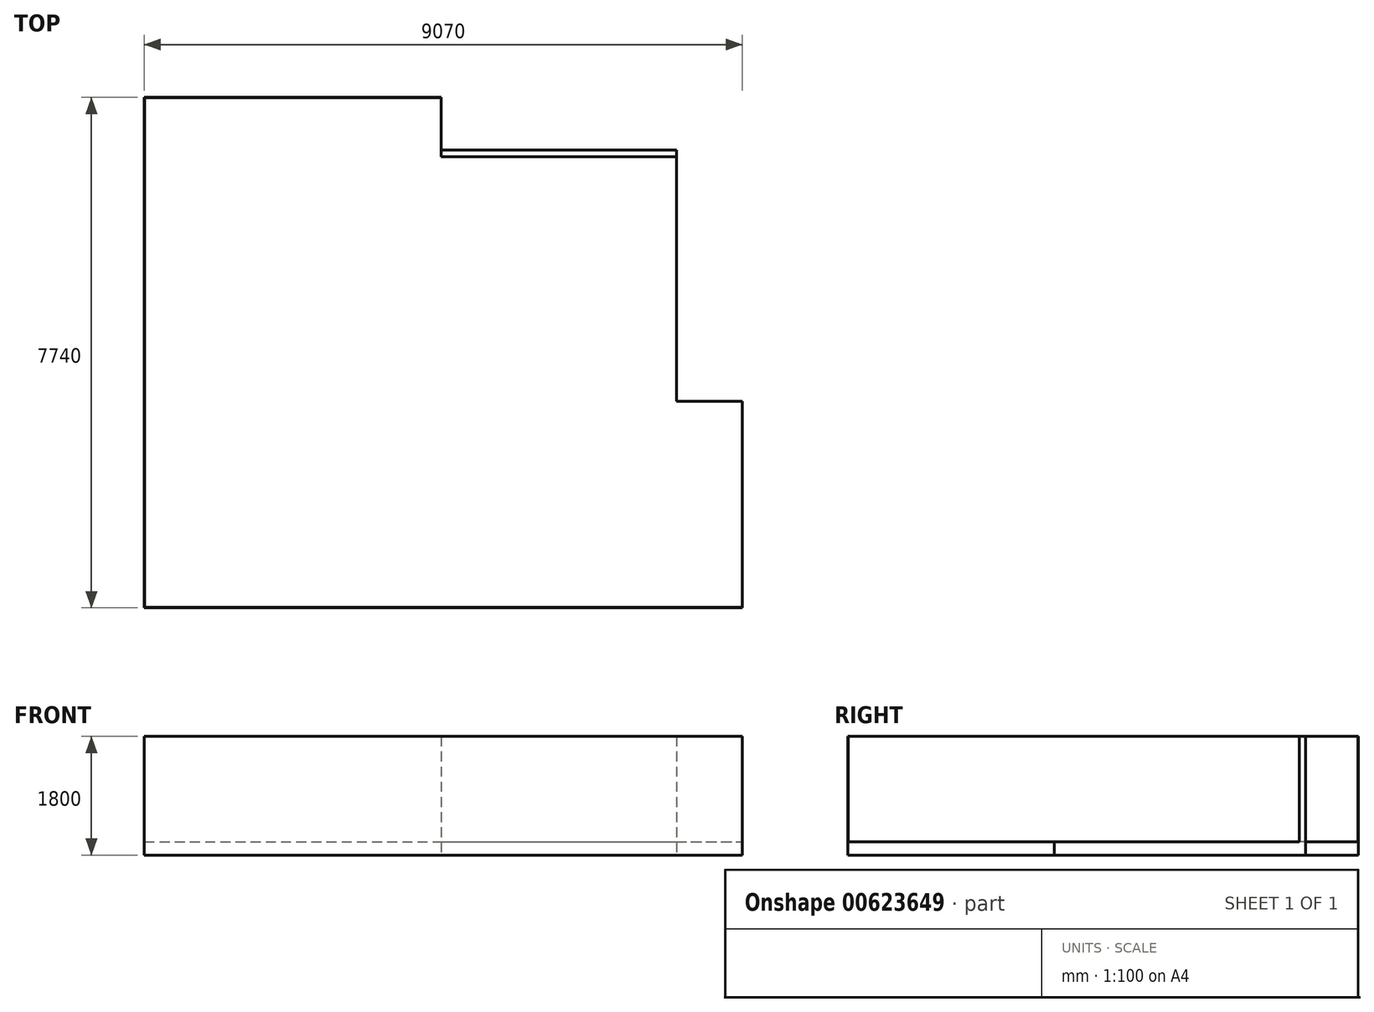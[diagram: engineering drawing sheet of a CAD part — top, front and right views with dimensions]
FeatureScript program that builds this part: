
annotation { "Feature Type Name" : "Feature", "Feature Type Description" : "" }
export const myFeature = defineFeature(function(context is Context, id is Id, definition is map)
    precondition{}
    {
        {
            var Q0;
            Q0=qCreatedBy(makeId("Top.planeOp"),FACE);
            var sketch = newSketch(context, id + "F0", { "sketchPlane" : qUnion([Q0])});
            skLineSegment(sketch, "E0", {"start": v(-109.76, -3110.31) * mm, "end": v(-109.76, 4629.69) * mm});
            skLineSegment(sketch, "E1", {"start": v(-109.76, -3110.31) * mm, "end": v(8960.24, -3110.31) * mm});
            skLineSegment(sketch, "E2", {"start": v(-109.76, 4629.69) * mm, "end": v(4390.24, 4629.69) * mm});
            skLineSegment(sketch, "E3", {"start": v(4390.24, 4629.69) * mm, "end": v(4390.24, 3729.69) * mm});
            skLineSegment(sketch, "E4", {"start": v(4390.24, 3729.69) * mm, "end": v(7960.24, 3729.69) * mm});
            skLineSegment(sketch, "E5", {"start": v(7960.24, 3729.69) * mm, "end": v(7960.24, 19.69) * mm});
            skLineSegment(sketch, "E6", {"start": v(8960.24, -3110.31) * mm, "end": v(8960.24, -3030.81) * mm});
            skLineSegment(sketch, "E7", {"start": v(8960.24, -3110.31) * mm, "end": v(8960.24, 19.69) * mm});
            skLineSegment(sketch, "E8", {"start": v(7960.24, 19.69) * mm, "end": v(8960.24, 19.69) * mm});
            skLineSegment(sketch, "E9.0", {"start": v(-104.76, 4624.69) * mm, "end": v(4390.24, 4624.69) * mm});
            skLineSegment(sketch, "E9.1", {"start": v(-104.76, -3105.31) * mm, "end": v(-104.76, 4624.69) * mm});
            skLineSegment(sketch, "E9.2", {"start": v(-104.76, -3105.31) * mm, "end": v(8960.24, -3105.31) * mm});
            skLineSegment(sketch, "E10.0", {"start": v(-504.76, 5024.69) * mm, "end": v(4390.24, 5024.69) * mm});
            skLineSegment(sketch, "E10.1", {"start": v(-504.76, -3505.31) * mm, "end": v(-504.76, 5024.69) * mm});
            skLineSegment(sketch, "E10.2", {"start": v(-504.76, -3505.31) * mm, "end": v(8960.24, -3505.31) * mm});
            skLineSegment(sketch, "E11.0", {"start": v(4390.24, 3829.69) * mm, "end": v(7960.24, 3829.69) * mm});
            skLineSegment(sketch, "E12", {"start": v(4390.24, 4624.69) * mm, "end": v(4390.24, 5024.69) * mm});
            skLineSegment(sketch, "E13", {"start": v(7960.24, 3729.69) * mm, "end": v(7960.24, 3829.69) * mm});
            skLineSegment(sketch, "E14", {"start": v(8960.24, -3505.31) * mm, "end": v(8960.24, -3105.31) * mm});
            skSolve(sketch);
        }
        {
            var Q0;
            {var subQ0=sQuery(id+"F0.wireOp",EDGE,"E4");Q0=makeQuery(id+"F0.imprint","IMPRINT",FACE,{"disambiguationData":[TD([[makeQuery(id+"F0.imprint","IMPRINT",EDGE,{"derivedFrom":subQ0}),-1.0]])]});}
            extrude(context, id + "F1", {"entities" : qUnion([Q0]), "depth" : 200 * mm, "offsetDistance" : 25 * mm});
        }
        {
            var Q0;
            {var subQ2=sQuery(id+"F0.wireOp",EDGE,"E9.0");Q0=makeQuery(id+"F0.imprint","IMPRINT",FACE,{"disambiguationData":[TD([[makeQuery(id+"F0.imprint","IMPRINT",EDGE,{"derivedFrom":subQ2}),1.0]])]});}
            extrude(context, id + "F2", {"entities" : qUnion([Q0]), "operationType" : NewBodyOperationType.ADD, "depth" : 1800 * mm, "offsetDistance" : 25 * mm});
        }
        {
            var Q0;
            {var subQ0=sQuery(id+"F0.wireOp",EDGE,"E4");Q0=makeQuery(id+"F0.imprint","IMPRINT",FACE,{"disambiguationData":[TD([[makeQuery(id+"F0.imprint","IMPRINT",EDGE,{"derivedFrom":subQ0}),1.0]])]});}
            extrude(context, id + "F3", {"entities" : qUnion([Q0]), "operationType" : NewBodyOperationType.ADD, "depth" : 1800 * mm, "offsetDistance" : 25 * mm});
        }
    });
